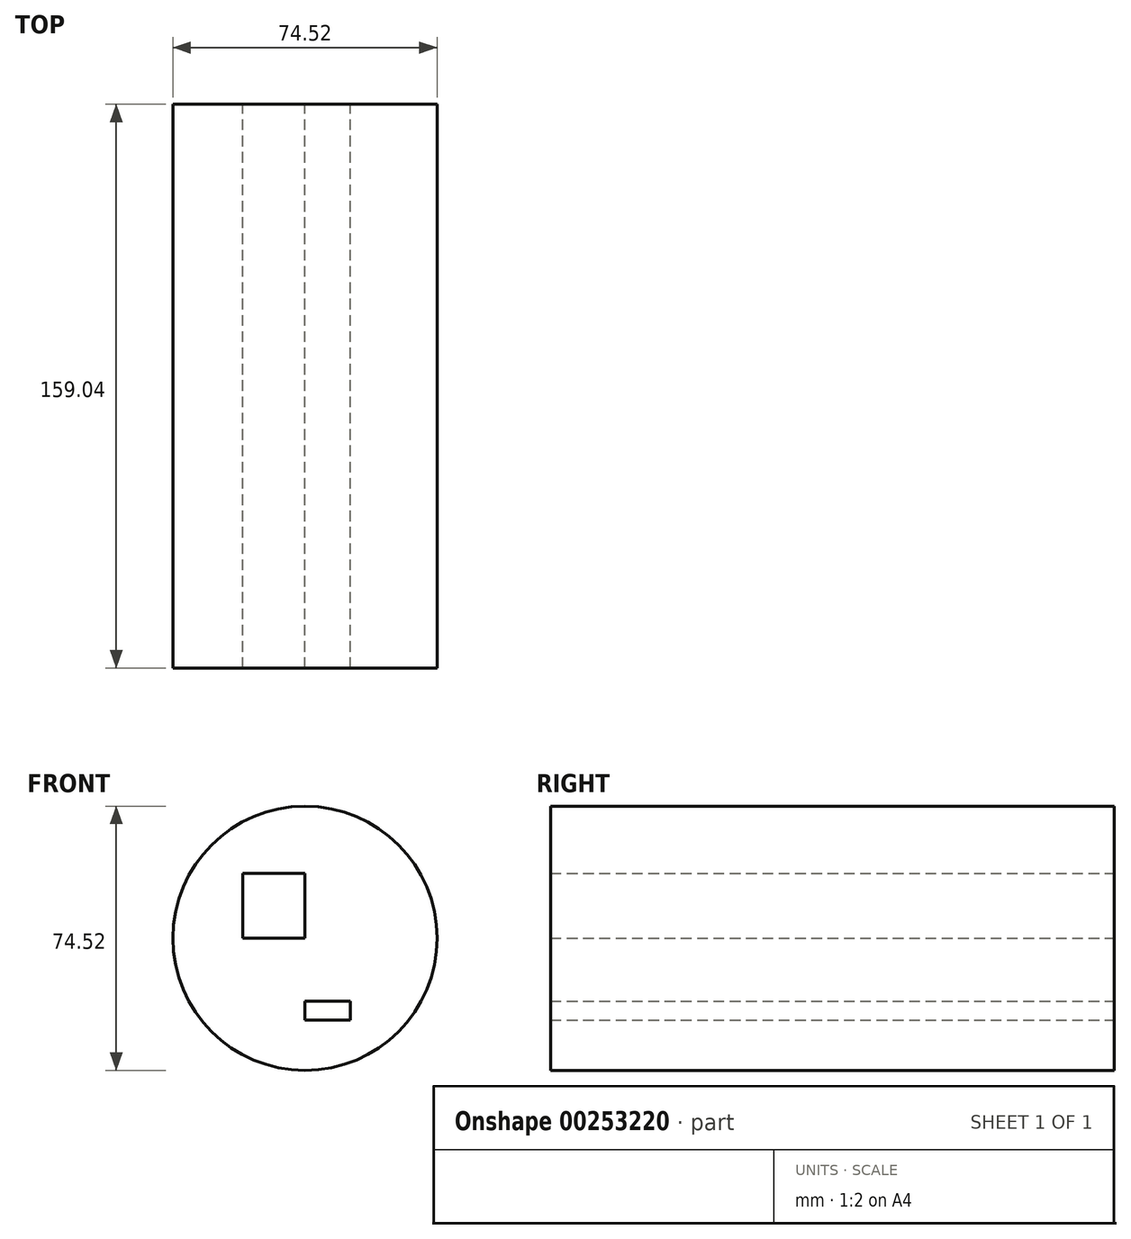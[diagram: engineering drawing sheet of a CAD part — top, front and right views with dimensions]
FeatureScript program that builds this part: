
annotation { "Feature Type Name" : "Feature", "Feature Type Description" : "" }
export const myFeature = defineFeature(function(context is Context, id is Id, definition is map)
    precondition{}
    {
        {
            var Q0;
            Q0=qCreatedBy(makeId("Front.planeOp"),FACE);
            var sketch = newSketch(context, id + "F0", { "sketchPlane" : qUnion([Q0])});
            skCircle(sketch, "E0", {"center": v(0, 0) * mm, "radius": 37.26 * mm});
            skLineSegment(sketch, "E1.bottom", {"start": v(-17.54, 18.37) * mm, "end": v(0, 18.37) * mm});
            skLineSegment(sketch, "E1.top", {"start": v(-17.54, 0) * mm, "end": v(0, 0) * mm});
            skLineSegment(sketch, "E1.left", {"start": v(-17.54, 18.37) * mm, "end": v(-17.54, 0) * mm});
            skLineSegment(sketch, "E1.right", {"start": v(0, 18.37) * mm, "end": v(0, 0) * mm});
            skLineSegment(sketch, "E2.bottom", {"start": v(0, -17.72) * mm, "end": v(12.8, -17.72) * mm});
            skLineSegment(sketch, "E2.top", {"start": v(0, -23.1) * mm, "end": v(12.8, -23.1) * mm});
            skLineSegment(sketch, "E2.left", {"start": v(0, -17.72) * mm, "end": v(0, -23.1) * mm});
            skLineSegment(sketch, "E2.right", {"start": v(12.8, -17.72) * mm, "end": v(12.8, -23.1) * mm});
            skSolve(sketch);
        }
        {
            var Q0;
            Q0=makeQuery(id+"F0.imprint","IMPRINT",FACE,{"disambiguationData":[TD([[makeQuery(id+"F0.imprint","IMPRINT",EDGE,{"derivedFrom":sQuery(id+"F0.wireOp",EDGE,"E0")}),1.0]])]});
            extrude(context, id + "F1", {"entities" : qUnion([Q0]), "depth" : 159.04 * mm});
        }
    });
